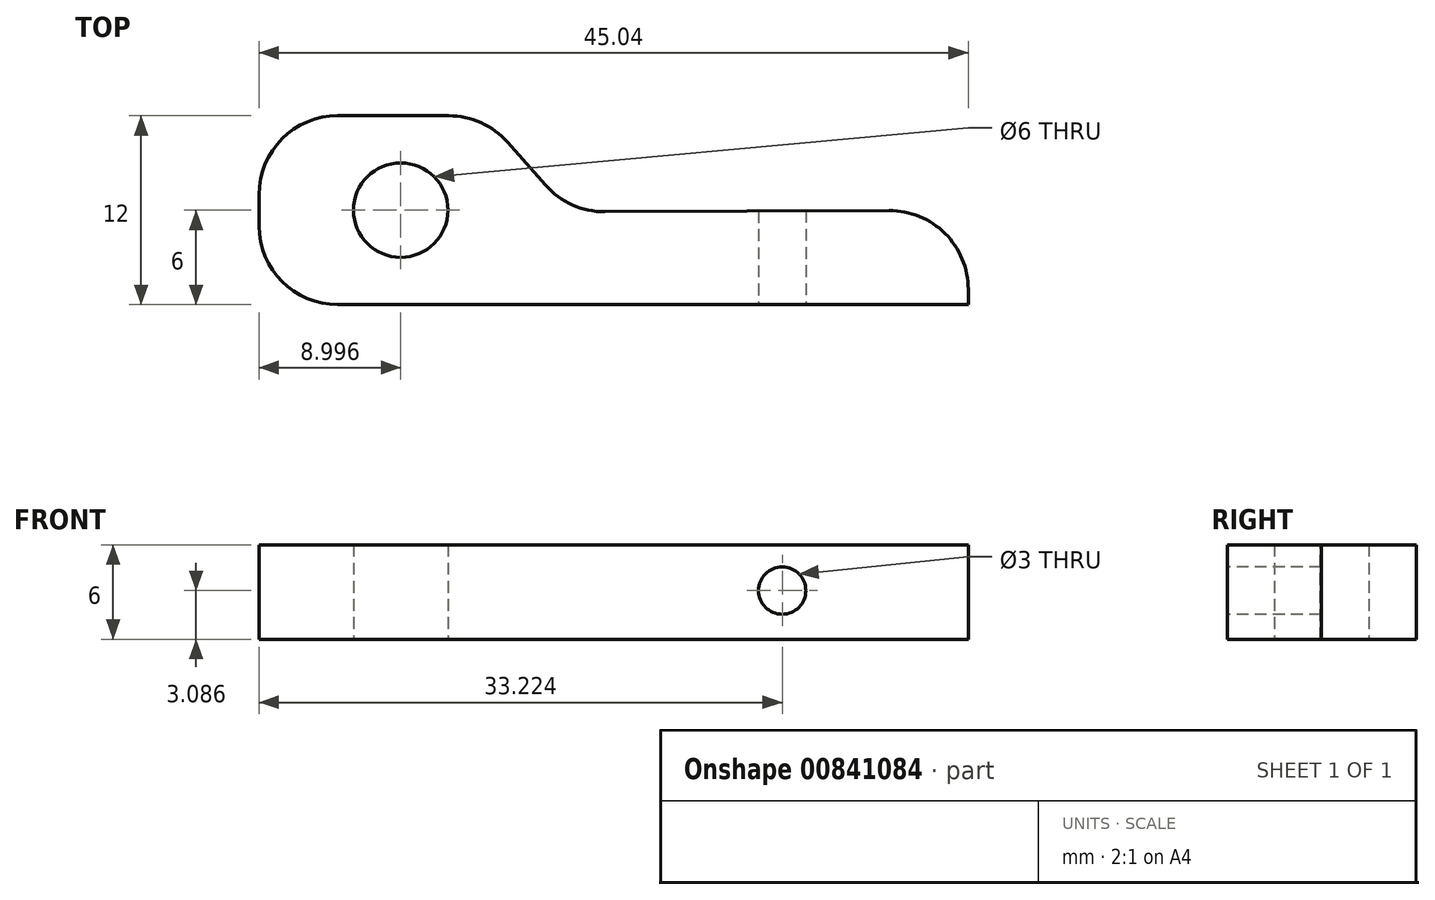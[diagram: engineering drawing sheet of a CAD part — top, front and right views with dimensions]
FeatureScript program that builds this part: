
annotation { "Feature Type Name" : "Feature", "Feature Type Description" : "" }
export const myFeature = defineFeature(function(context is Context, id is Id, definition is map)
    precondition{}
    {
        {
            var Q0;
            Q0=qCreatedBy(makeId("Top.planeOp"),FACE);
            var sketch = newSketch(context, id + "F0", { "sketchPlane" : qUnion([Q0])});
            skLineSegment(sketch, "E0.bottom", {"start": v(-19.7, 0) * mm, "end": v(25.35, 0) * mm});
            skLineSegment(sketch, "E0.top", {"start": v(-19.7, 12) * mm, "end": v(-5.4, 12) * mm});
            skLineSegment(sketch, "E0.left", {"start": v(-19.7, 0) * mm, "end": v(-19.7, 12) * mm});
            skLineSegment(sketch, "E0.right", {"start": v(25.35, 0) * mm, "end": v(25.35, 6) * mm});
            skLineSegment(sketch, "E1", {"start": v(-10.7, 3) * mm, "end": v(-10.7, 0) * mm, "construction": true});
            skLineSegment(sketch, "E2", {"start": v(-19.7, 6) * mm, "end": v(-13.7, 6) * mm, "construction": true});
            skPoint(sketch, "E3.orphan", {"position": v(-10.7, 12) * mm});
            skPoint(sketch, "E4", {"position": v(-10.7, 6) * mm});
            skCircle(sketch, "E5", {"center": v(-10.7, 6) * mm, "radius": 3 * mm});
            skLineSegment(sketch, "E6", {"start": v(0, 5.9) * mm, "end": v(25.35, 6) * mm});
            skLineSegment(sketch, "E7", {"start": v(-5.4, 12) * mm, "end": v(0, 5.9) * mm});
            skSolve(sketch);
        }
        {
            var Q0;
            Q0=qCreatedBy(makeId("Front.planeOp"),FACE);
            var sketch = newSketch(context, id + "F1", { "sketchPlane" : qUnion([Q0])});
            skLineSegment(sketch, "E8", {"start": v(13.53, 6.17) * mm, "end": v(13.53, 0) * mm});
            skPoint(sketch, "E9", {"position": v(13.53, 3.09) * mm});
            skSolve(sketch);
        }
        {
            var Q0;
            Q0 = qSketchRegion(id + "F0", true);
            extrude(context, id + "F2", {"entities" : qUnion([Q0]), "depth" : 6 * mm, "offsetDistance" : 25 * mm});
        }
        {
            var Q0;
            Q0=sQuery(id+"F1.wireOp",VERTEX,"E9");
            var Q1;
            Q1=makeQuery(id+"F2.opExtrude","SWEPT_BODY",BODY,{"disambiguationData":[OSD([sQuery(id+"F0.wireOp",EDGE,"E0.bottom"),sQuery(id+"F0.wireOp",EDGE,"E0.top"),sQuery(id+"F0.wireOp",EDGE,"E0.left"),sQuery(id+"F0.wireOp",EDGE,"E0.right"),sQuery(id+"F0.wireOp",EDGE,"E5"),sQuery(id+"F0.wireOp",EDGE,"E6"),sQuery(id+"F0.wireOp",EDGE,"E7")])]});
            hole(context, id + "F3", {"style" : HoleStyle.SIMPLE, "endStyle" : HoleEndStyle.THROUGH, "holeDiameter" : 3 * mm, "majorDiameter" : 5 * mm, "isTappedThrough" : true, "tappedDepth" : 12 * mm, "tapClearance" : 3, "locations" : qUnion([Q0]), "scope" : qUnion([Q1])});
        }
        {
            var Q0;
            Q0=makeQuery(id+"F2.opExtrude","SWEPT_EDGE",EDGE,{"disambiguationData":[OSD([sQuery(id+"F0.wireOp",EDGE,"E0.top"),sQuery(id+"F0.wireOp",EDGE,"E0.left")])]});
            var Q1;
            Q1=makeQuery(id+"F2.opExtrude","SWEPT_EDGE",EDGE,{"disambiguationData":[OSD([sQuery(id+"F0.wireOp",EDGE,"E0.bottom"),sQuery(id+"F0.wireOp",EDGE,"E0.left")])]});
            fillet(context, id + "F4", {"entities" : qUnion([Q0, Q1]), "radius" : 5 * mm, "tangentPropagation" : true, "allowEdgeOverflow" : false});
        }
        {
            var Q0;
            Q0=makeQuery(id+"F2.opExtrude","SWEPT_EDGE",EDGE,{"disambiguationData":[OSD([sQuery(id+"F0.wireOp",EDGE,"E0.top"),sQuery(id+"F0.wireOp",EDGE,"E7")])]});
            fillet(context, id + "F5", {"entities" : qUnion([Q0]), "radius" : 5 * mm, "tangentPropagation" : true, "allowEdgeOverflow" : false});
        }
        {
            var Q0;
            Q0=makeQuery(id+"F2.opExtrude","SWEPT_EDGE",EDGE,{"disambiguationData":[OSD([sQuery(id+"F0.wireOp",EDGE,"E6"),sQuery(id+"F0.wireOp",EDGE,"E7")])]});
            fillet(context, id + "F6", {"entities" : qUnion([Q0]), "radius" : 5 * mm, "tangentPropagation" : true, "allowEdgeOverflow" : false});
        }
        {
            var Q0;
            Q0=makeQuery(id+"F2.opExtrude","SWEPT_EDGE",EDGE,{"disambiguationData":[OSD([sQuery(id+"F0.wireOp",EDGE,"E0.right"),sQuery(id+"F0.wireOp",EDGE,"E6")])]});
            fillet(context, id + "F7", {"entities" : qUnion([Q0]), "radius" : 5 * mm, "tangentPropagation" : true, "allowEdgeOverflow" : false});
        }
    });
